# Revit family: 00-5678-05-DC
name_source: partatom
category: Luminarias
revit_build: Autodesk Revit 2017 (Build: 20160225_1515(x64)
units: mm (PartAtom-declared; Revit-internal decimal feet)

## family parameters
Anfitrión = Cara
Compartido = Sí
Corte con vacíos al cargar = No
Cota de conector redondo = Diámetro de uso
Número OmniClass = 23.80.70.00
Origen de luz = No
Punto de cálculo de habitación = No
Tipo de pieza = Normal
Título OmniClass = Lighting

## types (1)
- 00-5678-05-DC
    Acabado = Negro, Cemento
    CRI = 0
    Carga aparente = 0 VA
    Catálogo = Decorative
    CodigoGubimclass = 50.60.50.20
    CodigoOmniclass = 21-04 50 40
    CodigoUniclass2015 = EF_70_80
    CodigoUniformat2010 = D5040
    DescripcionGubimclass = Iluminación interior
    DescripcionOmniclass = Lighting
    DescripcionUniclass2015 = Lighting
    DescripcionUniformat2010 = Lighting
    EAN13 = 8435381456146
    Eficiencia energética = NO BULB
    Elevación por defecto = 1000 mm  [stored 3.28084 ft]
    Etiqueta V/f = 220-240V/50-60Hz
    Fabricante = LEDS C4
    Familia = Eclipse Conic
    FechaVersion = Julio 2020
    Ficha = http://files.leds-c4.com
    Fotometría = http://files.leds-c4.com
    IMC = http://files.leds-c4.com
    IP = IP20
    IfcExportAs = IfcLightFixture
IfcLightFixture
    IfcExportType = NOTDEFINED
    Imagen web = http://files.leds-c4.com
    LDT = http://files.leds-c4.com
    Lumenes reales (lm) = 0
    Material = Acero, Cemento
    Peso neto (KG) = 1.2
    Pluma comercial = http://files.leds-c4.com
    Producto descatalogado = Catalogado ES
    Referencia = 00-5678-05-DC
    Tender text (Castellano) = LEDS C4
Eclipse Conic
00-5678-05-DCV1

Colgante de uso interior para iluminar hacia abajo. 
Material estructura: Acero, Cemento. Acabado estructura: Negro, Cemento. Garantía: 5 Años.

Peso neto del producto (Kg): 1.200
Longitud del producto (mm): Ø100
Altura del producto (mm): Max 1825

Clase 2. IP: IP20. E27. Longitud máxima de la bombilla que admite la luminaria: 140. Diámetro máximo de la bombilla que admite la luminaria: 60. Nº de portalámparas o Leds: 1. Potencia máxima de la fuente de luz: 20W. Equipo incluido: No. Potencia total: 20.
    Tender text (English) = LEDS C4
Eclipse Conic
00-5678-05-DCV1

Pendant for indoor use. 

For downlighting. Structure material: Steel, cement. Structure finish: Black, Cement. Warranty: 5 Years.

Product net weight (Kg): 1.200
Product length (mm): Ø100
Product height (mm): Max 1825

Class 2. IP: IP20. E27. Maximum length of luminaire bulb: 140. Maximum diameter of luminaire bulb: 60. No. of lampholders or LEDs: 1. Maximum power of light source: 20W. Gear included: No. Total power: 20.
    Tipo = Colgante
    Vatios (W) = 20
    Versión = v1

note: [stored X ft] marks values corroborated as IEEE doubles in the binary element streams (Revit-internal decimal feet)
